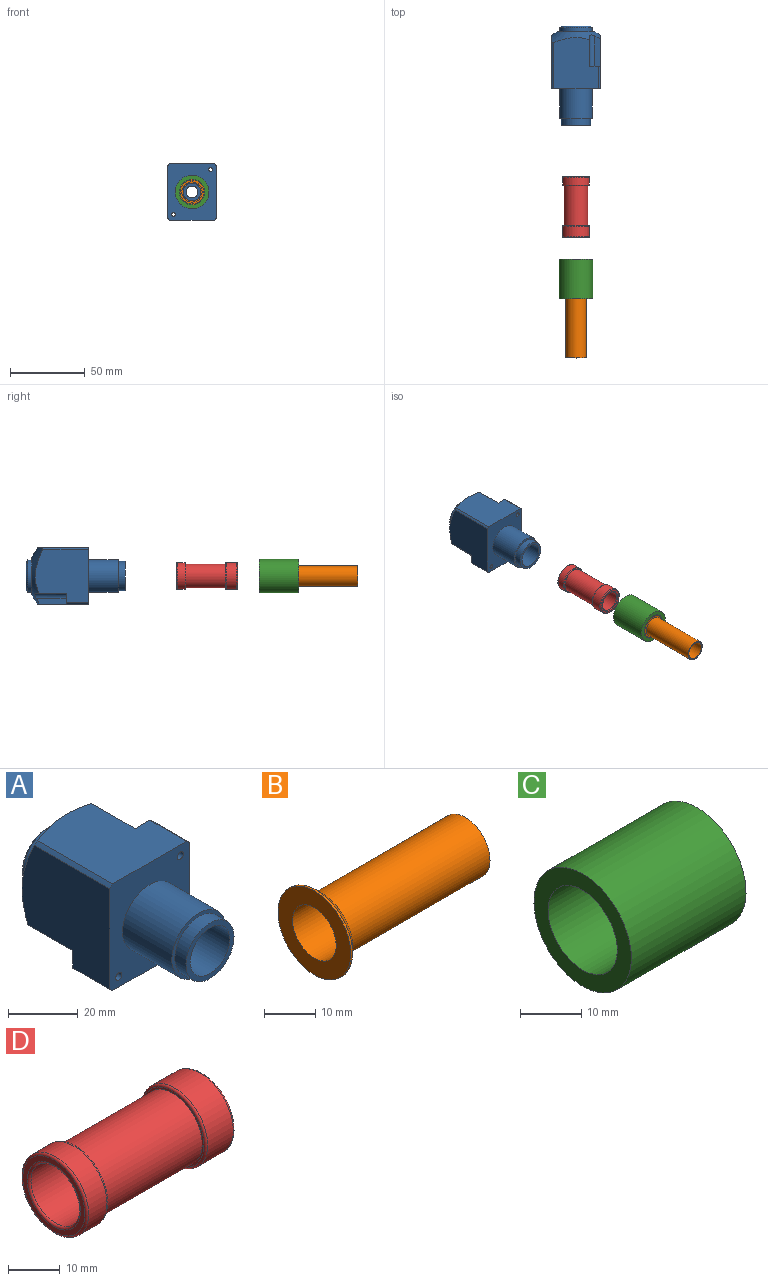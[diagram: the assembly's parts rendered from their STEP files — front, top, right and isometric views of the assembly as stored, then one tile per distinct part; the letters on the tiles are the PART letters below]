
ASSEMBLY  parts=4 mates=5
PART A: 33 faces, bbox 48.2x66.4x48.2 mm
  f0: cone r=24mm half-angle=57deg, axis (0,-1,0), area 748.2mm2, adj f3,f4,f5,f14,f15,f20,f21,f23
  f1: cylinder r=24mm len=14.9mm, axis (0,-1,0), area 24.9mm2, adj f3,f6,f21,f22
  f2: cylinder r=24mm len=14.9mm, axis (0,-1,0), area 24.9mm2, adj f4,f6,f20,f26
  f3: plane 35.57x35.33mm, normal (-1,0,0), area 1087.5mm2, adj f0,f1,f6,f15,f22,f25
  f4: plane 35.57x35.33mm, normal (1,0,0), area 1087.5mm2, adj f0,f2,f5,f6,f26,f27
  f5: cylinder r=24mm len=30.53mm, axis (0,-1,0), area 51mm2, adj f0,f4,f6,f21
  f6: plane 37.5x32.5mm, normal (0,-1,0), area 826.1mm2, adj f1,f2,f3,f4,f5,f15,f16,f20
  f7: cylinder r=8mm len=16mm, axis (0,-1,0), area 754mm2, adj f8,f19
  f8: plane 16x16mm, normal (0,-1,0), area 88mm2, adj f7,f9
  f9: cylinder r=6mm len=35mm, axis (0,-1,0), area 1319.5mm2, adj f8,f10
  f10: plane 12x12mm, normal (0,-1,0), area 62.8mm2, adj f9,f11
  f11: cylinder r=4mm len=16.2mm, axis (0,-1,0), area 407.2mm2, adj f10,f12
  f12: plane 19.8x19.8mm, normal (0,1,0), area 257.6mm2, adj f11,f32
  f13: cylinder r=10.9mm len=21.8mm, axis (0,-1,0), area 184.9mm2, adj f14,f32
  f14: plane 25x25mm, normal (0,1,0), area 117.6mm2, adj f0,f13
  f15: cylinder r=24mm len=30.53mm, axis (0,-1,0), area 51mm2, adj f0,f3,f6,f20
  f16: cylinder r=11mm len=22mm, axis (0,-1,0), area 1382.3mm2, adj f6,f17
  f17: plane 22x22mm, normal (0,-1,0), area 81.5mm2, adj f16,f18
  f18: cylinder r=9.75mm len=19.5mm, axis (0,-1,0), area 275.7mm2, adj f17,f19
  f19: plane 19.5x19.5mm, normal (0,-1,0), area 97.6mm2, adj f7,f18
  f20: plane 33.95x29.97mm, normal (0,0,1), area 881.1mm2, adj f0,f2,f6,f15,f26,f29
  f21: plane 33.95x29.97mm, normal (0,0,-1), area 881.1mm2, adj f0,f1,f5,f6,f22,f24
  f22: plane 7.25x7.25mm, normal (0,1,0), area 44.4mm2, adj f1,f3,f21,f23,f24,f25,f31
  f23: cylinder r=3.5mm len=20.81mm, axis (0,1,0), area 112.9mm2, adj f0,f22,f24,f25
  f24: plane 20.02x3.91mm, normal (-1,0,0), area 70.5mm2, adj f0,f21,f22,f23
  f25: plane 20.4x3.96mm, normal (0,0,-1), area 72.2mm2, adj f0,f3,f22,f23
  f26: plane 7.25x7.25mm, normal (0,1,0), area 44.3mm2, adj f2,f4,f20,f27,f28,f29,f30
  f27: plane 20.34x3.86mm, normal (0,0,1), area 70.3mm2, adj f0,f4,f26,f28
  f28: cylinder r=3.5mm len=20.81mm, axis (0,1,0), area 114.7mm2, adj f0,f26,f27,f29
  f29: plane 20.02x3.91mm, normal (1,0,0), area 70.5mm2, adj f0,f20,f26,f28
  f30: cylinder r=1.25mm len=14.9mm, axis (0,1,0), area 117mm2, adj f6,f26
  f31: cylinder r=1.25mm len=14.9mm, axis (0,1,0), area 117mm2, adj f6,f22
  f32: cone r=10.9mm half-angle=45deg, axis (0,-1,0), area 92.4mm2, adj f12,f13
PART B: 7 faces, bbox 41.5x20x20 mm
  f0: plane 17x17mm, normal (1,0,0), area 83.8mm2, adj f1,f6
  f1: cone r=10mm half-angle=45deg, axis (-1,0,0), area 123.3mm2, adj f0,f2
  f2: cylinder r=10mm len=20mm, axis (-1,0,0), area 31.4mm2, adj f1,f3
  f3: plane 20x20mm, normal (-1,0,0), area 201.1mm2, adj f2,f4
  f4: cylinder r=6mm len=41.5mm, axis (-1,0,0), area 1564.5mm2, adj f3,f5
  f5: plane 13.5x13.5mm, normal (1,0,0), area 30mm2, adj f4,f6
  f6: cylinder r=6.75mm len=39.5mm, axis (-1,0,0), area 1675.3mm2, adj f0,f5
PART C: 4 faces, bbox 26.5x22.5x22.5 mm
  f0: plane 22.5x22.5mm, normal (-1,0,0), area 196.5mm2, adj f1,f3
  f1: cylinder r=8mm len=26.5mm, axis (-1,0,0), area 1332mm2, adj f0,f2
  f2: plane 22.5x22.5mm, normal (1,0,0), area 196.5mm2, adj f1,f3
  f3: cylinder r=11.25mm len=26.5mm, axis (-1,0,0), area 1873.2mm2, adj f0,f2
PART D: 14 faces, bbox 40.5x19.5x19.5 mm
  f0: plane 17x17mm, normal (1,0,0), area 61.9mm2, adj f1,f13
  f1: torus R=8.5mm, axis (-1,0,0), area 43.5mm2, adj f0,f2
  f2: cylinder r=9mm len=18mm, axis (-1,0,0), area 395.8mm2, adj f1,f3
  f3: torus R=8.5mm, axis (-1,0,0), area 43.5mm2, adj f2,f4
  f4: plane 17x17mm, normal (-1,0,0), area 25.9mm2, adj f3,f5
  f5: cylinder r=8mm len=26.5mm, axis (-1,0,0), area 1332mm2, adj f4,f6
  f6: plane 17x17mm, normal (1,0,0), area 25.9mm2, adj f5,f7
  f7: torus R=8.5mm, axis (-1,0,0), area 43.5mm2, adj f6,f8
  f8: cylinder r=9mm len=18mm, axis (-1,0,0), area 282.7mm2, adj f7,f9
  f9: torus R=8.5mm, axis (-1,0,0), area 43.5mm2, adj f8,f10
  f10: plane 17x17mm, normal (-1,0,0), area 61.9mm2, adj f9,f11
  f11: torus R=7.25mm, axis (-1,0,0), area 34.2mm2, adj f10,f12
  f12: cylinder r=6.75mm len=39.5mm, axis (-1,0,0), area 1675.3mm2, adj f11,f13
  f13: torus R=7.25mm, axis (-1,0,0), area 34.2mm2, adj f0,f12
PLACE A t=(-13.12,34.11,-32.02)mm fixed
PLACE B rot(axis=(-0.01,0.01,-1),90deg) t=(-13.12,-92.52,-32.02)mm
PLACE C rot(axis=(-0.67,-0.67,0.3),146.7deg) t=(-13.12,-82.02,-32.02)mm
PLACE D rot(axis=(-0.02,0.02,-1),90deg) t=(-13.12,-6.51,-32.02)mm
MATE revolute C.f1 <-> B.f1  axis (0,-1,0) through (-13.12,-82.02,-32.02)mm
MATE cylindrical A.f0 <-> C.f1  axis (0,-1,0) through (-13.12,34.11,-32.02)mm
MATE ball A.f0 <-> A.f0  axis (0,1,0) through (-13.12,100.31,-32.02)mm
MATE cylindrical D.f1 <-> C.f1  axis (0,1,0) through (-13.12,-33.51,-32.02)mm
MATE parallel C.f1 <-> D.f1  axis (0,1,0) through (-13.12,-55.52,-32.02)mm
